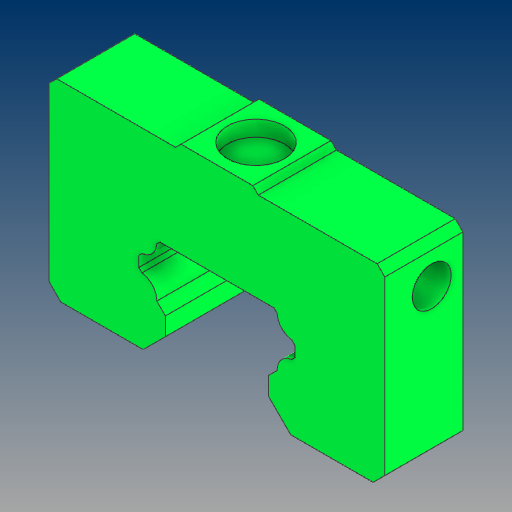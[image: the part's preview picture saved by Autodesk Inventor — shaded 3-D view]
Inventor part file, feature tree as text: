
AUTODESK INVENTOR PART (.ipt)
format: ipt  version: 2021 (Build 250183000, 183)  size: 177,152 bytes
history: native  units: mm
features: extrude x3, sketch x3, projected_geometry x2, mirror x1
ambient origin geometry x8: Origin, YZ Plane, XZ Plane, XY Plane, X Axis, Y Axis, Z Axis, Center Point
bodies: Solid1 (feature_tree)
feature tree (9):
  extrude  "Extrusion1"  Depth=6.7mm TaperAngle=0.0deg
  extrude  "Extrusion2"  [1 undecoded]
  mirror  "Mirror1"
  extrude  "Extrusion3"  [1 undecoded]
  sketch  "Sketch1"  dims[d0=10.0mm d1=0.0mm d2=6.7mm d3=0.0mm]
  sketch  "Sketch2"  dims[d4=2.0mm d5=0.0mm]
  projected_geometry  "Projected Loop1"
  sketch  "Sketch3"
  projected_geometry  "Projected Loop2"
note: 2 required parameter values undecoded (feature->parameter linkage not recoverable at this tier; creation-order binding heuristic only, values carry confidence <= 0.55)
